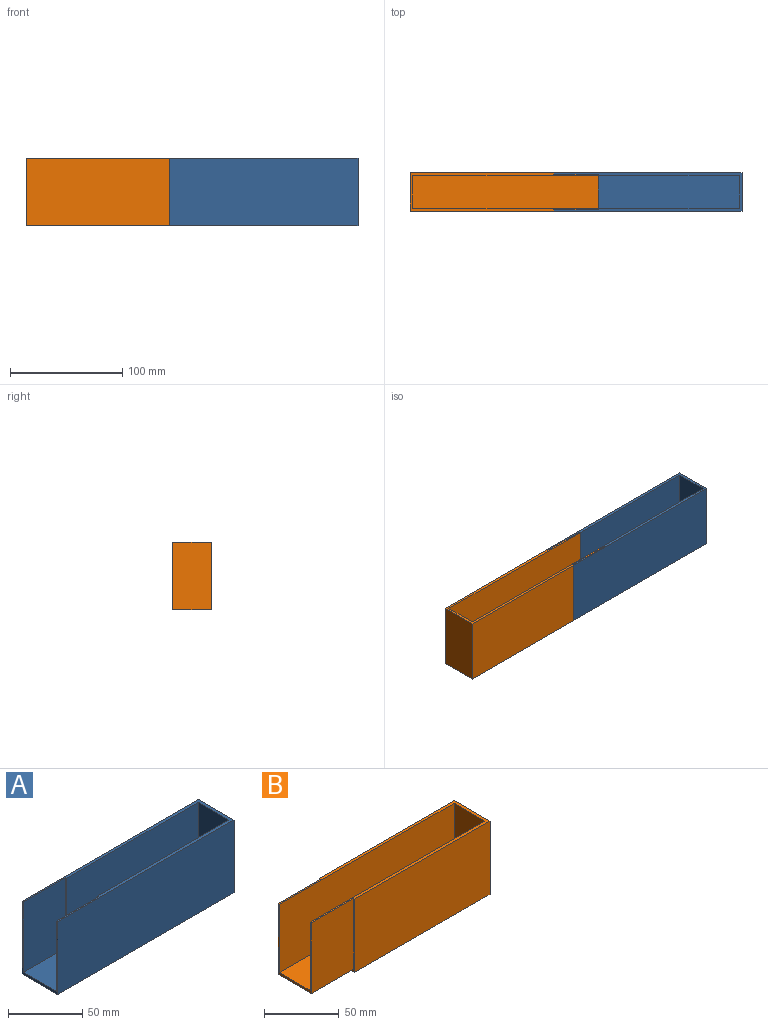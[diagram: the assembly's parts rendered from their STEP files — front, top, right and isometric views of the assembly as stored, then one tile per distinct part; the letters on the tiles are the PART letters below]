
ASSEMBLY  parts=2 mates=1
PART A: 14 faces, bbox 167.8x34x60 mm
  f0: plane 125.4x29.2mm, normal (0,0,1), area 3661.7mm2, adj f4,f5,f6,f7
  f1: plane 167.8x60mm, normal (0,1,0), area 10068mm2, adj f2,f10,f11,f12
  f2: plane 60x34mm, normal (-1,0,0), area 207.2mm2, adj f1,f3,f8,f9,f11,f12,f13
  f3: plane 58x40mm, normal (0,-1,0), area 2320mm2, adj f2,f7,f11,f13
  f4: plane 125.4x56mm, normal (0,-1,0), area 7022.4mm2, adj f0,f5,f7,f11
  f5: plane 56x29.2mm, normal (-1,0,0), area 1635.2mm2, adj f0,f4,f6,f11
  f6: plane 125.4x56mm, normal (0,1,0), area 7022.4mm2, adj f0,f5,f7,f11
  f7: plane 58x31.6mm, normal (-1,0,0), area 197.6mm2, adj f0,f3,f4,f6,f8,f11,f13
  f8: plane 58x40mm, normal (0,1,0), area 2320mm2, adj f2,f7,f11,f13
  f9: plane 167.8x60mm, normal (0,-1,0), area 10068mm2, adj f2,f10,f11,f12
  f10: plane 60x34mm, normal (1,0,0), area 2040mm2, adj f1,f9,f11,f12
  f11: plane 167.8x34mm, normal (0,0,1), area 779.5mm2, adj f1,f2,f3,f4,f5,f6,f7,f8
  f12: plane 167.8x34mm, normal (0,0,-1), area 5705.2mm2, adj f1,f2,f9,f10
  f13: plane 40x31.6mm, normal (0,0,1), area 1264mm2, adj f2,f3,f7,f8
PART B: 14 faces, bbox 167.8x34x60 mm
  f0: plane 58x40mm, normal (0,-1,0), area 2320mm2, adj f1,f8,f11,f13
  f1: plane 58x31.6mm, normal (-1,0,0), area 197.6mm2, adj f0,f5,f7,f10,f11,f12,f13
  f2: plane 127.8x60mm, normal (0,-1,0), area 7668mm2, adj f4,f8,f9,f11
  f3: plane 127.8x60mm, normal (0,1,0), area 7668mm2, adj f4,f8,f9,f11
  f4: plane 127.8x34mm, normal (0,0,-1), area 4345.2mm2, adj f2,f3,f8,f9
  f5: plane 165.4x56mm, normal (0,-1,0), area 9262.4mm2, adj f1,f6,f11,f12
  f6: plane 56x29.2mm, normal (-1,0,0), area 1635.2mm2, adj f5,f7,f11,f12
  f7: plane 165.4x56mm, normal (0,1,0), area 9262.4mm2, adj f1,f6,f11,f12
  f8: plane 60x34mm, normal (-1,0,0), area 207.2mm2, adj f0,f2,f3,f4,f10,f11,f13
  f9: plane 60x34mm, normal (1,0,0), area 2040mm2, adj f2,f3,f4,f11
  f10: plane 58x40mm, normal (0,1,0), area 2320mm2, adj f1,f8,f11,f13
  f11: plane 167.8x34mm, normal (0,0,1), area 779.5mm2, adj f0,f1,f2,f3,f5,f6,f7,f8
  f12: plane 165.4x29.2mm, normal (0,0,1), area 4829.7mm2, adj f1,f5,f6,f7
  f13: plane 40x31.6mm, normal (0,0,-1), area 1264mm2, adj f0,f1,f8,f10
PLACE A t=(23.23,65.08,40.96)mm
PLACE B rot(axis=(0,0,1),180deg) t=(-104.57,65.08,40.96)mm
MATE fastened B.f1 <-> A.f7  axis (1,0,0) through (-20.67,65.08,40.96)mm
